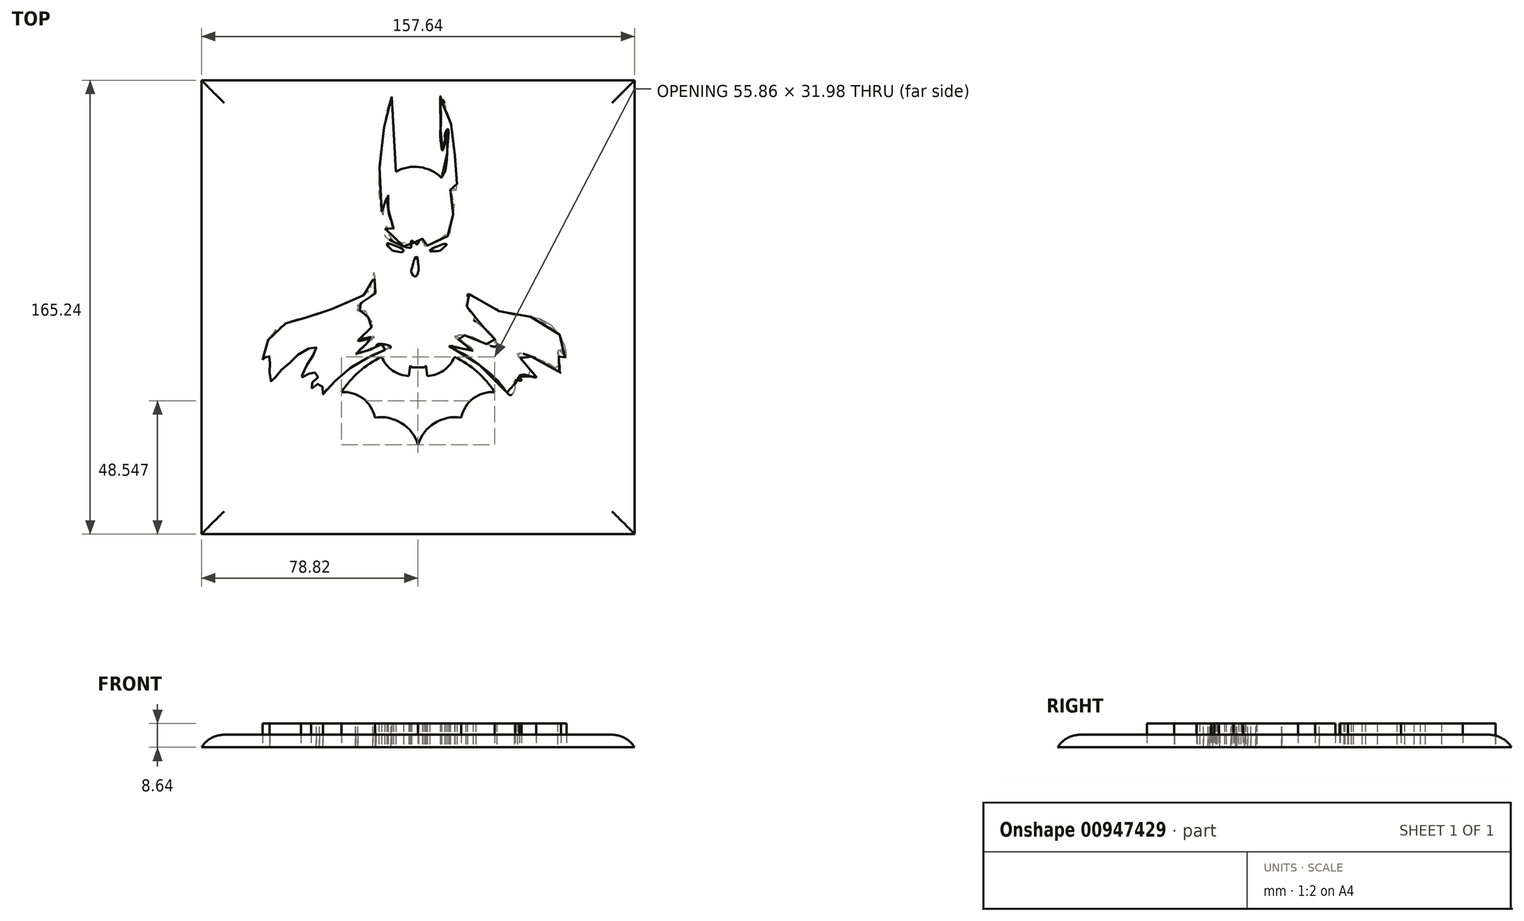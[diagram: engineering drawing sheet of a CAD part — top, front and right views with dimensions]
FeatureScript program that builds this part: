
annotation { "Feature Type Name" : "Feature", "Feature Type Description" : "" }
export const myFeature = defineFeature(function(context is Context, id is Id, definition is map)
    precondition{}
    {
        {
            var Q0;
            Q0=qCreatedBy(makeId("Top.planeOp"),FACE);
            var sketch = newSketch(context, id + "F0", { "sketchPlane" : qUnion([Q0])});
            skFitSpline(sketch, "E0", {"points": [v(-56.53, -36.48) * mm, v(-55.75, -32.96) * mm, v(-53.4, -27.3) * mm, v(-48.52, -23.38) * mm, v(-44.42, -21.63) * mm, v(-38.27, -20.6) * mm, v(-30.35, -17.52) * mm, v(-18.82, -12.44) * mm, v(-17.08, -10.12) * mm, v(-16.73, -7.45) * mm, v(-16.03, -4.66) * mm, v(-15.8, -7.1) * mm, v(-15.57, -10) * mm, v(-15.34, -11.75) * mm, v(-16.5, -13.26) * mm, v(-19.98, -15.35) * mm, v(-21.96, -16.63) * mm, v(-22.77, -18.14) * mm, v(-21.15, -18.37) * mm, v(-19.29, -18.48) * mm, v(-18.7, -19.76) * mm, v(-17.78, -21.62) * mm, v(-17.08, -22.43) * mm, v(-16.38, -23.83) * mm, v(-18.36, -25.8) * mm, v(-20.8, -28.48) * mm, v(-21.84, -29.52) * mm, v(-19.17, -29.06) * mm, v(-17.08, -28.01) * mm, v(-15.57, -27.9) * mm, v(-18.24, -30.22) * mm, v(-20.22, -31.84) * mm, v(-21.96, -33.36) * mm, v(-22.66, -34.98) * mm, v(-19.98, -33.59) * mm, v(-15.74, -32.23) * mm, v(-14.99, -31.03) * mm, v(-12.43, -30.8) * mm, v(-9.88, -31.84) * mm, v(-12.43, -33) * mm, v(-16.27, -34.4) * mm, v(-19.75, -36.6) * mm, v(-23.7, -38.58) * mm, v(-26.5, -41.14) * mm, v(-29.86, -43.93) * mm, v(-33.23, -47.3) * mm, v(-34.6, -49.06) * mm], "startDerivative": vector(28.5, 138.58) * mm, "endDerivative": vector(-63.28, -87.8) * mm});
            skFitSpline(sketch, "E1", {"points": [v(-34.6, -49.06) * mm, v(-34.6, -47.2) * mm, v(-35.17, -45.52) * mm, v(-36.5, -45.28) * mm, v(-38.25, -46.5) * mm, v(-38.83, -46.85) * mm, v(-38.72, -45.57) * mm, v(-37.84, -43.48) * mm, v(-35.93, -42.36) * mm, v(-37.61, -41.1) * mm, v(-38.77, -40.98) * mm, v(-40.8, -42.09) * mm, v(-42.14, -42.9) * mm, v(-42.6, -43.37) * mm, v(-41.91, -41.5) * mm, v(-39.76, -37.1) * mm, v(-37.38, -33.55) * mm, v(-37.09, -31.98) * mm, v(-38.54, -31.98) * mm, v(-43.3, -34.3) * mm, v(-46.5, -37.5) * mm, v(-49.81, -40.23) * mm, v(-51.67, -42.5) * mm, v(-53.24, -44.59) * mm, v(-53.93, -42.96) * mm, v(-54.05, -39.7) * mm, v(-53.93, -36.98) * mm, v(-54, -35.81) * mm, v(-54.52, -34.6) * mm, v(-55.62, -35.58) * mm, v(-55.97, -36.8) * mm, v(-56.53, -36.48) * mm], "startDerivative": vector(2.91, 58.26) * mm, "endDerivative": vector(-36.25, 31.82) * mm});
            skArc(sketch, "E2", {"start": v(-13.3, -35.4) * mm, "mid": v(-21.48, -40.85) * mm, "end": v(-27.93, -48.28) * mm});
            skArc(sketch, "E3", {"start": v(-15.74, -57.5) * mm, "mid": v(-20.06, -50.55) * mm, "end": v(-27.93, -48.28) * mm});
            skArc(sketch, "E4", {"start": v(0, -67.38) * mm, "mid": v(-6.04, -59.52) * mm, "end": v(-15.74, -57.5) * mm});
            skArc(sketch, "E5", {"start": v(-13.3, -35.4) * mm, "mid": v(-9.3, -40.32) * mm, "end": v(-3.32, -42.36) * mm});
            skLineSegment(sketch, "E6", {"start": v(-2.38, -39.23) * mm, "end": v(0, -39.23) * mm});
            skLineSegment(sketch, "E7", {"start": v(-2.38, -39.23) * mm, "end": v(-2.83, -38.59) * mm});
            skLineSegment(sketch, "E8", {"start": v(-2.83, -38.59) * mm, "end": v(-3.32, -42.36) * mm});
            skLineSegment(sketch, "E9.MirrorCS", {"start": v(2.38, -39.23) * mm, "end": v(0, -39.23) * mm});
            skLineSegment(sketch, "E10.MirrorCS", {"start": v(2.83, -38.59) * mm, "end": v(3.32, -42.36) * mm});
            skArc(sketch, "E11.MirrorCS", {"start": v(13.3, -35.4) * mm, "mid": v(9.3, -40.32) * mm, "end": v(3.32, -42.36) * mm});
            skArc(sketch, "E12.MirrorCS", {"start": v(13.3, -35.4) * mm, "mid": v(21.48, -40.85) * mm, "end": v(27.93, -48.28) * mm});
            skArc(sketch, "E13.MirrorCS", {"start": v(15.74, -57.5) * mm, "mid": v(20.06, -50.55) * mm, "end": v(27.93, -48.28) * mm});
            skArc(sketch, "E14.MirrorCS", {"start": v(0, -67.38) * mm, "mid": v(6.04, -59.52) * mm, "end": v(15.74, -57.5) * mm});
            skLineSegment(sketch, "E15.MirrorCS", {"start": v(2.38, -39.23) * mm, "end": v(2.83, -38.59) * mm});
            skFitSpline(sketch, "E16", {"points": [v(11.36, -31.55) * mm, v(16.07, -34.1) * mm, v(22.98, -38.89) * mm, v(29.8, -45.06) * mm, v(33.45, -49.4) * mm, v(34.43, -48.85) * mm, v(35.3, -47.2) * mm, v(35.24, -45.68) * mm, v(35.12, -44.23) * mm, v(36.17, -43.9) * mm, v(37.56, -43.99) * mm, v(37.36, -43.22) * mm, v(36.88, -42.32) * mm, v(38.35, -41.93) * mm, v(40.44, -42.3) * mm, v(43.01, -42.82) * mm, v(41.71, -40.8) * mm, v(39.24, -37.93) * mm, v(37.17, -35.9) * mm, v(36.14, -34.99) * mm, v(36.43, -34.1) * mm, v(39.07, -34.54) * mm, v(44.35, -36.4) * mm, v(50.16, -39.6) * mm, v(51.89, -41.2) * mm, v(51.97, -39.76) * mm, v(51.65, -37.4) * mm, v(51.2, -35.26) * mm, v(50.8, -32.76) * mm, v(51.57, -32.5) * mm, v(52.6, -33.83) * mm, v(53.76, -35.91) * mm, v(54, -33.77) * mm, v(52.11, -28.36) * mm, v(47.57, -23.19) * mm, v(41.26, -20.82) * mm, v(35.06, -20.19) * mm, v(29.92, -18.88) * mm, v(23.68, -15.54) * mm, v(18.47, -12.52) * mm, v(18.18, -12.5) * mm, v(18.02, -13.07) * mm, v(17.98, -14.38) * mm, v(18.02, -15.77) * mm, v(17.74, -16.99) * mm, v(17.36, -17.33) * mm, v(18.02, -18.27) * mm, v(19.97, -19.78) * mm, v(20.98, -20.98) * mm, v(20.7, -21.62) * mm, v(20, -21.72) * mm, v(20.9, -22.55) * mm, v(23, -24) * mm, v(24.9, -25.54) * mm, v(25.34, -25.86) * mm, v(27.2, -27.72) * mm, v(27.55, -28.13) * mm, v(28.32, -29.62) * mm, v(28.65, -31.16) * mm, v(27.82, -31.7) * mm, v(25.78, -31.16) * mm, v(23.8, -30.26) * mm, v(20.68, -28.56) * mm, v(17.3, -27.56) * mm, v(16.35, -27.54) * mm, v(15.12, -27.47) * mm, v(13.51, -27.6) * mm, v(13.53, -28.44) * mm, v(16.18, -29.75) * mm, v(17.92, -31.08) * mm, v(19.76, -32.15) * mm, v(19.83, -33.14) * mm, v(14.9, -31.82) * mm, v(12.67, -31.46) * mm, v(11.36, -31.55) * mm]});
            skFitSpline(sketch, "E17", {"points": [v(-9.59, 59.3) * mm, v(-11.29, 54.57) * mm, v(-12.56, 46.22) * mm, v(-13.74, 36) * mm, v(-14.13, 23) * mm, v(-12.8, 16.48) * mm, v(-12.3, 19.14) * mm, v(-11.32, 22.5) * mm, v(-11, 23.47) * mm, v(-10.83, 22.47) * mm, v(-10.85, 20.42) * mm, v(-10.68, 16.82) * mm, v(-9.87, 14.41) * mm, v(-9, 12.25) * mm, v(-9.07, 10.89) * mm, v(-10, 11.05) * mm, v(-11.08, 11.65) * mm, v(-11.52, 12.14) * mm, v(-11.9, 11.26) * mm, v(-12.08, 9.17) * mm, v(-11.55, 8.04) * mm, v(-2.76, 4.31) * mm, v(-2.6, 5.63) * mm, v(-2.45, 6.8) * mm, v(-1.62, 6.51) * mm, v(-0.38, 5.58) * mm, v(0, 6.09) * mm, v(0.35, 6.89) * mm, v(0.83, 7.59) * mm, v(1.54, 7.63) * mm, v(1.68, 6.72) * mm, v(1.62, 5.94) * mm, v(1.7, 5.3) * mm, v(1.89, 4.7) * mm, v(3.97, 5.46) * mm, v(7.6, 7.5) * mm, v(9.73, 8.22) * mm, v(11.6, 8.97) * mm, v(11.67, 11.23) * mm, v(12.77, 16.47) * mm, v(13.08, 21.48) * mm, v(11.87, 24.7) * mm, v(12.02, 26.34) * mm, v(13.21, 25.63) * mm, v(13.83, 25.05) * mm, v(14.15, 28.08) * mm, v(14.1, 32.84) * mm, v(13.34, 38.55) * mm, v(12.93, 43.43) * mm, v(10.94, 53.39) * mm, v(8.23, 59.5) * mm, v(8.19, 56.19) * mm, v(8.23, 48.18) * mm, v(8.06, 45.83) * mm, v(8.43, 41.4) * mm, v(8.82, 39.74) * mm, v(9.84, 42.76) * mm, v(9.88, 46.08) * mm, v(10.87, 47.59) * mm, v(10.98, 44.82) * mm, v(10.64, 40.13) * mm, v(9.85, 32.4) * mm, v(8.7, 30.2) * mm, v(8.56, 29.8) * mm], "startDerivative": vector(-86.18, -202.64) * mm, "endDerivative": vector(-13, -57.4) * mm});
            skArc(sketch, "E18", {"start": v(8.56, 29.8) * mm, "mid": v(0.63, 33.68) * mm, "end": v(-8.06, 32.04) * mm});
            skLineSegment(sketch, "E19", {"start": v(-8.06, 32.04) * mm, "end": v(-9.59, 59.3) * mm});
            skFitSpline(sketch, "E20", {"points": [v(-11.31, 5.83) * mm, v(-9.87, 5.6) * mm, v(-7.42, 4.68) * mm, v(-5.28, 3.47) * mm, v(-5.7, 2.79) * mm, v(-8.42, 3.1) * mm, v(-9.87, 3.74) * mm, v(-11.31, 5.83) * mm]});
            skFitSpline(sketch, "E21", {"points": [v(4.2, 3.2) * mm, v(5.19, 4.02) * mm, v(7.92, 5.23) * mm, v(9.74, 5.76) * mm, v(10.44, 5.54) * mm, v(9.45, 4.52) * mm, v(8.18, 3.43) * mm, v(6.15, 3.04) * mm, v(4.2, 3.2) * mm]});
            skFitSpline(sketch, "E22", {"points": [v(-0.5, 1.2) * mm, v(-1.34, 0) * mm, v(-2, -2.37) * mm, v(-2.44, -3.89) * mm, v(-2.17, -5.14) * mm, v(-1.07, -6.19) * mm, v(0, -4.74) * mm, v(0, -1.2) * mm, v(-0.16, 0.32) * mm, v(-0.5, 1.2) * mm]});
            skLineSegment(sketch, "E23.bottom", {"start": v(78.82, -99.94) * mm, "end": v(-78.82, -99.94) * mm});
            skLineSegment(sketch, "E23.top", {"start": v(78.82, 65.3) * mm, "end": v(-78.82, 65.3) * mm});
            skLineSegment(sketch, "E23.left", {"start": v(78.82, -99.94) * mm, "end": v(78.82, 65.3) * mm});
            skLineSegment(sketch, "E23.right", {"start": v(-78.82, -99.94) * mm, "end": v(-78.82, 65.3) * mm});
            skPoint(sketch, "E23.middle", {"position": v(0, -17.32) * mm});
            skSolve(sketch);
        }
        {
            var Q0;
            Q0=makeQuery(id+"F0.imprint","IMPRINT",FACE,{"disambiguationData":[TD([[makeQuery(id+"F0.imprint","IMPRINT",EDGE,{"derivedFrom":sQuery(id+"F0.wireOp",EDGE,"E17")}),1.0]])]});
            var Q1;
            Q1=makeQuery(id+"F0.imprint","IMPRINT",FACE,{"disambiguationData":[TD([[makeQuery(id+"F0.imprint","IMPRINT",EDGE,{"derivedFrom":sQuery(id+"F0.wireOp",EDGE,"E20")}),-1.0]])]});
            var Q2;
            Q2=makeQuery(id+"F0.imprint","IMPRINT",FACE,{"disambiguationData":[TD([[makeQuery(id+"F0.imprint","IMPRINT",EDGE,{"derivedFrom":sQuery(id+"F0.wireOp",EDGE,"E21")}),-1.0]])]});
            var Q3;
            Q3=makeQuery(id+"F0.imprint","IMPRINT",FACE,{"disambiguationData":[TD([[makeQuery(id+"F0.imprint","IMPRINT",EDGE,{"derivedFrom":sQuery(id+"F0.wireOp",EDGE,"E22")}),1.0]])]});
            var Q4;
            Q4=makeQuery(id+"F0.imprint","IMPRINT",FACE,{"disambiguationData":[TD([[makeQuery(id+"F0.imprint","IMPRINT",EDGE,{"derivedFrom":sQuery(id+"F0.wireOp",EDGE,"E0")}),-1.0]])]});
            var Q5;
            Q5=makeQuery(id+"F0.imprint","IMPRINT",FACE,{"disambiguationData":[TD([[makeQuery(id+"F0.imprint","IMPRINT",EDGE,{"derivedFrom":sQuery(id+"F0.wireOp",EDGE,"E16")}),1.0]])]});
            var Q6;
            Q6=makeQuery(id+"F0.imprint","IMPRINT",FACE,{"disambiguationData":[TD([[makeQuery(id+"F0.imprint","IMPRINT",EDGE,{"derivedFrom":sQuery(id+"F0.wireOp",EDGE,"E2")}),1.0]])]});
            extrude(context, id + "F1", {"entities" : qUnion([Q0, Q1, Q2, Q3, Q4, Q5, Q6]), "depth" : 8.64 * mm, "offsetDistance" : 25.4 * mm});
        }
        {
            var Q0;
            Q0=makeQuery(id+"F0.imprint","IMPRINT",FACE,{"disambiguationData":[TD([[makeQuery(id+"F0.imprint","IMPRINT",EDGE,{"derivedFrom":sQuery(id+"F0.wireOp",EDGE,"E0")}),1.0]])]});
            extrude(context, id + "F2", {"entities" : qUnion([Q0]), "depth" : 4.57 * mm, "offsetDistance" : 25.4 * mm});
        }
        {
            var Q0;
            Q0=makeQuery(id+"F2.opExtrude","CAP_EDGE",EDGE,{"disambiguationData":[OSD([sQuery(id+"F0.wireOp",EDGE,"E23.bottom")])],"isStart":false});
            var Q1;
            Q1=makeQuery(id+"F2.opExtrude","CAP_EDGE",EDGE,{"disambiguationData":[OSD([sQuery(id+"F0.wireOp",EDGE,"E23.left")])],"isStart":false});
            var Q2;
            Q2=makeQuery(id+"F2.opExtrude","CAP_EDGE",EDGE,{"disambiguationData":[OSD([sQuery(id+"F0.wireOp",EDGE,"E23.top")])],"isStart":false});
            var Q3;
            Q3=makeQuery(id+"F2.opExtrude","CAP_EDGE",EDGE,{"disambiguationData":[OSD([sQuery(id+"F0.wireOp",EDGE,"E23.right")])],"isStart":false});
            fillet(context, id + "F3", {"entities" : qUnion([Q0, Q1, Q2, Q3]), "radius" : 9.8 * mm, "tangentPropagation" : true, "allowEdgeOverflow" : false});
        }
    });
